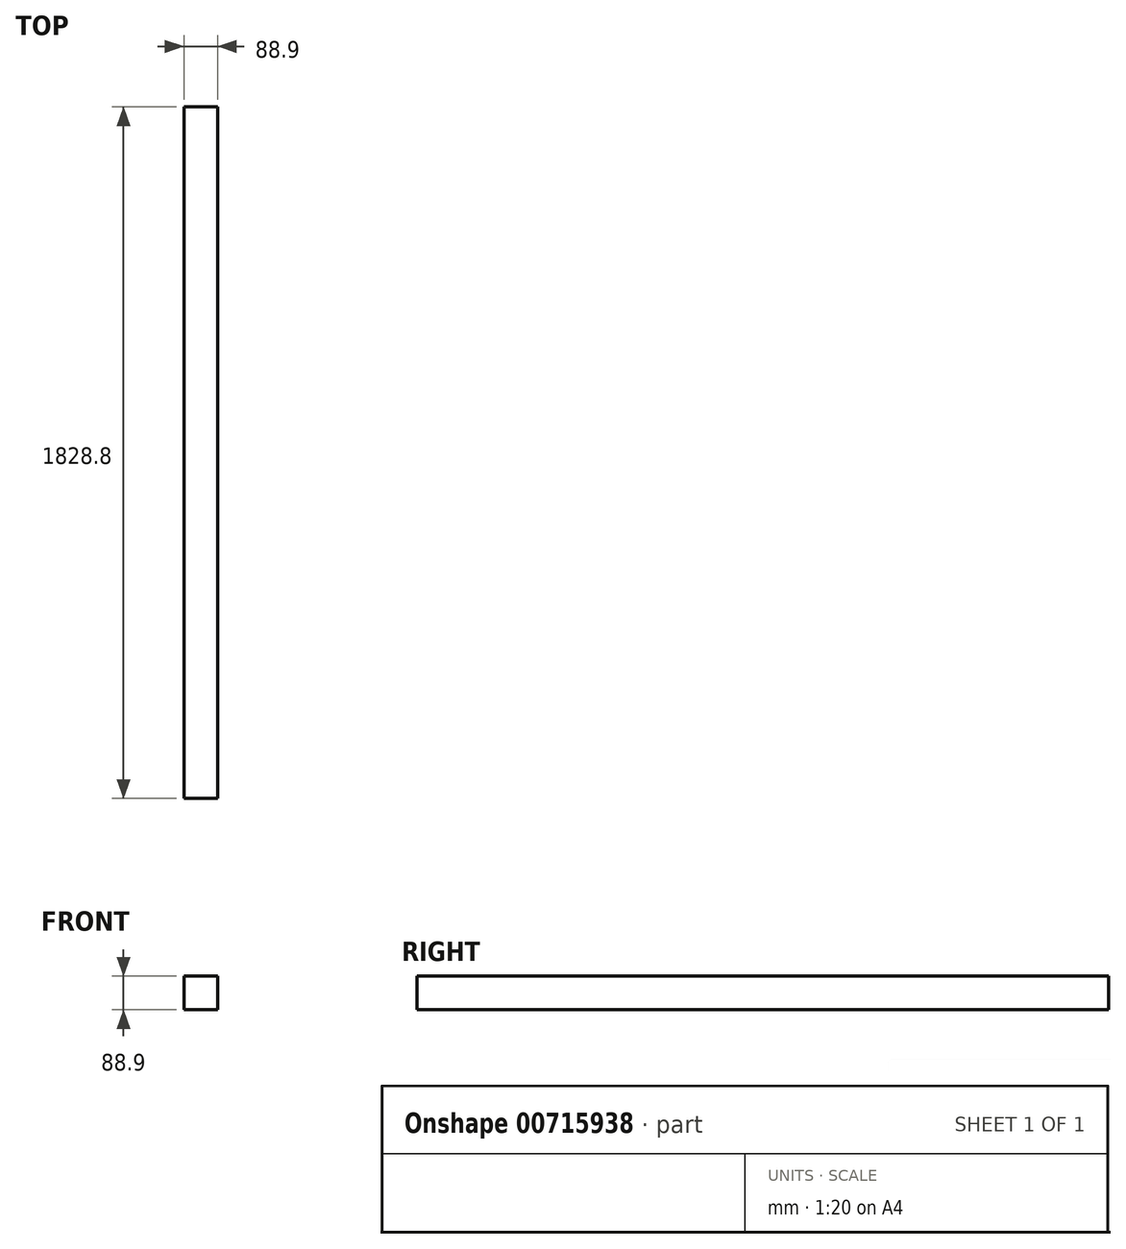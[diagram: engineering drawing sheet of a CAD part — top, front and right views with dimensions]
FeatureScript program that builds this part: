
annotation { "Feature Type Name" : "Feature", "Feature Type Description" : "" }
export const myFeature = defineFeature(function(context is Context, id is Id, definition is map)
    precondition{}
    {
        {
            var Q0;
            Q0=qCreatedBy(makeId("Front.planeOp"),FACE);
            var sketch = newSketch(context, id + "F0", { "sketchPlane" : qUnion([Q0])});
            skLineSegment(sketch, "E0.bottom", {"start": v(-44.45, -44.45) * mm, "end": v(44.45, -44.45) * mm});
            skLineSegment(sketch, "E0.top", {"start": v(-44.45, 44.45) * mm, "end": v(44.45, 44.45) * mm});
            skLineSegment(sketch, "E0.left", {"start": v(-44.45, -44.45) * mm, "end": v(-44.45, 44.45) * mm});
            skLineSegment(sketch, "E0.right", {"start": v(44.45, -44.45) * mm, "end": v(44.45, 44.45) * mm});
            skPoint(sketch, "E0.middle", {"position": v(0, 0) * mm});
            skSolve(sketch);
        }
        {
            var Q0;
            Q0=makeQuery(id+"F0.imprint","IMPRINT",FACE,{"disambiguationData":[TD([[makeQuery(id+"F0.imprint","IMPRINT",EDGE,{"derivedFrom":sQuery(id+"F0.wireOp",EDGE,"E0.bottom")}),1.0]])]});
            extrude(context, id + "F1", {"entities" : qUnion([Q0]), "endBound" : BoundingType.SYMMETRIC, "depth" : 1828.8 * mm, "offsetDistance" : 25.4 * mm});
        }
    });
